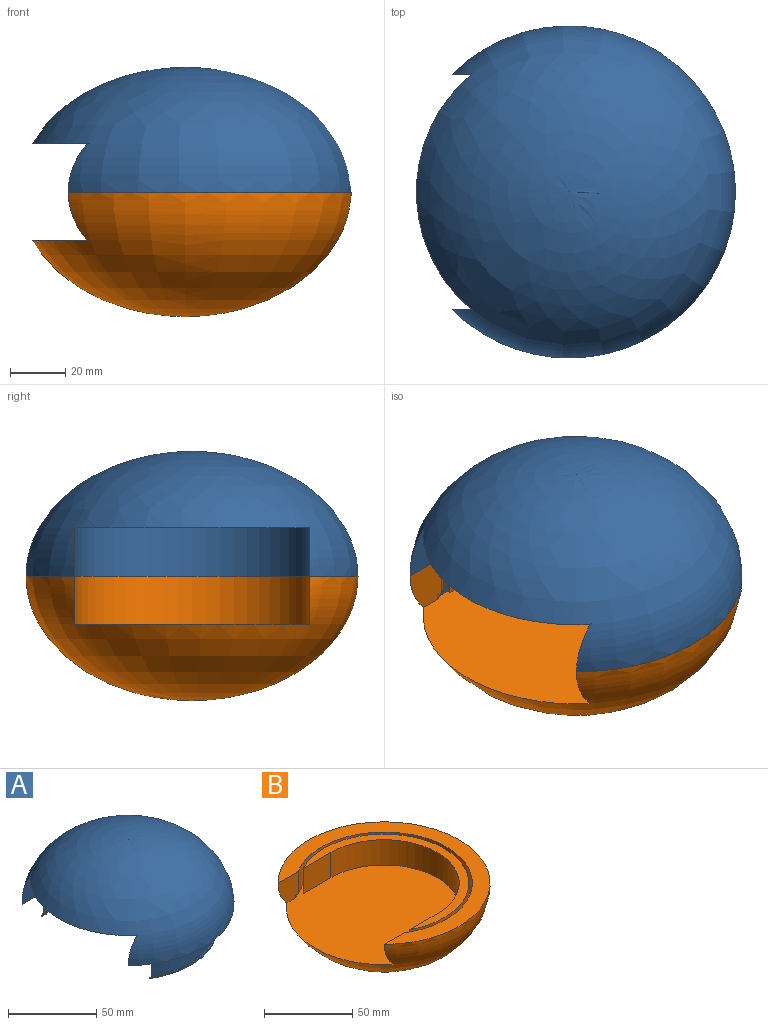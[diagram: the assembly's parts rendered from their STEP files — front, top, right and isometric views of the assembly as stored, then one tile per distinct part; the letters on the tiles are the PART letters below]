
ASSEMBLY  parts=2 mates=1
PART A: 13 faces, bbox 120x120x62 mm
  f0: plane 17x3.66mm, normal (0,-1,0), area 37.1mm2, adj f2,f3,f4,f5,f6,f12
  f1: plane 17x3.66mm, normal (0,1,0), area 37.1mm2, adj f2,f3,f4,f5,f6,f12
  f2: cylinder r=50.3mm len=100.6mm, axis (0,0,-1), area 212.9mm2, adj f0,f1,f5,f12
  f3: cylinder r=48.5mm len=97mm, axis (0,0,-1), area 3383.2mm2, adj f0,f1,f5,f6
  f4: cylinder r=49.5mm len=99mm, axis (0,0,-1), area 3309.1mm2, adj f0,f1,f6,f12
  f5: plane 100.6x76.4mm, normal (0,0,-1), area 370.8mm2, adj f0,f1,f2,f3
  f6: plane 120x102.35mm, normal (0,0,-1), area 3635.9mm2, adj f0,f1,f3,f4,f7,f9,f10,f11
  f7: cylinder r=42.5mm len=85mm, axis (0,0,1), area 2336.6mm2, adj f6,f8,f9,f10
  f8: plane 97.78x85mm, normal (0,0,-1), area 7019.3mm2, adj f7,f9,f10,f11
  f9: plane 42.36x17.5mm, normal (0,-1,0), area 701.8mm2, adj f6,f7,f8,f11
  f10: plane 42.36x17.5mm, normal (0,1,0), area 701.8mm2, adj f6,f7,f8,f11
  f11: revolved ~120x120mm, area 17214mm2, adj f6,f8,f9,f10
  f12: plane 100.6x76.4mm, normal (0,0,1), area 167.9mm2, adj f0,f1,f2,f4
PART B: 13 faces, bbox 120x120x45 mm
  f0: plane 17.5x16.02mm, normal (0,1,0), area 237.1mm2, adj f3,f4,f5,f10,f11,f12
  f1: plane 17.5x16.02mm, normal (0,-1,0), area 237.1mm2, adj f3,f4,f5,f10,f11,f12
  f2: plane 96x70.31mm, normal (0,0,1), area 947.4mm2, adj f6,f7,f8,f9
  f3: plane 120x102.35mm, normal (0,0,1), area 2481.5mm2, adj f0,f1,f5,f10
  f4: plane 106.28x102mm, normal (0,0,1), area 7645.5mm2, adj f0,f1,f5,f6,f7,f8,f9,f11
  f5: revolved ~120x120mm, area 17214mm2, adj f0,f1,f3,f4
  f6: plane 22.31x17.5mm, normal (0,1,0), area 390.4mm2, adj f2,f4,f8,f9
  f7: plane 22.31x17.5mm, normal (0,-1,0), area 390.4mm2, adj f2,f4,f8,f9
  f8: cylinder r=42.5mm len=85mm, axis (0,0,1), area 2336.6mm2, adj f2,f4,f6,f7
  f9: cylinder r=48mm len=96mm, axis (0,0,-1), area 3451.1mm2, adj f2,f4,f6,f7
  f10: cylinder r=50mm len=100mm, axis (0,0,-1), area 3294.7mm2, adj f0,f1,f3,f12
  f11: cylinder r=51mm len=102mm, axis (0,0,-1), area 439.9mm2, adj f0,f1,f4,f12
  f12: plane 102x79.19mm, normal (0,0,-1), area 216.3mm2, adj f0,f1,f10,f11
PLACE A t=(38.68,-68.3,46.86)mm
PLACE B t=(38.68,-68.3,46.86)mm
MATE revolute B.f8 <-> A.f7  axis (0,0,1) through (38.68,-68.3,46.86)mm
